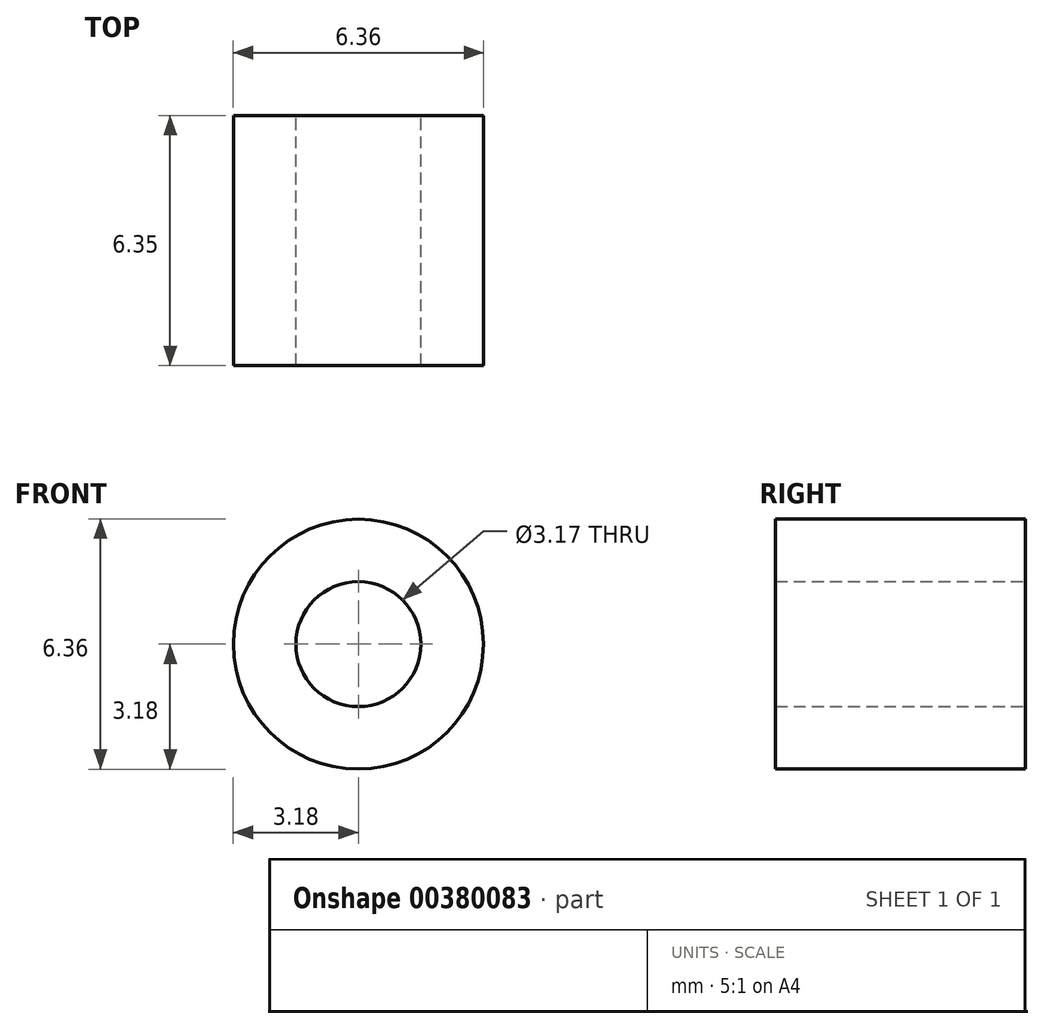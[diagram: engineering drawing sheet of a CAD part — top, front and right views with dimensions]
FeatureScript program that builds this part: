
annotation { "Feature Type Name" : "Feature", "Feature Type Description" : "" }
export const myFeature = defineFeature(function(context is Context, id is Id, definition is map)
    precondition{}
    {
        {
            var Q0;
            Q0=qCreatedBy(makeId("Front.planeOp"),FACE);
            var sketch = newSketch(context, id + "F0", { "sketchPlane" : qUnion([Q0])});
            skCircle(sketch, "E0", {"center": v(0, 0) * mm, "radius": 1.59 * mm});
            skCircle(sketch, "E1", {"center": v(0, 0) * mm, "radius": 3.18 * mm});
            skSolve(sketch);
        }
        {
            var Q0;
            Q0 = qSketchRegion(id + "F0", true);
            extrude(context, id + "F1", {"entities" : qUnion([Q0]), "depth" : 6.35 * mm});
        }
    });
